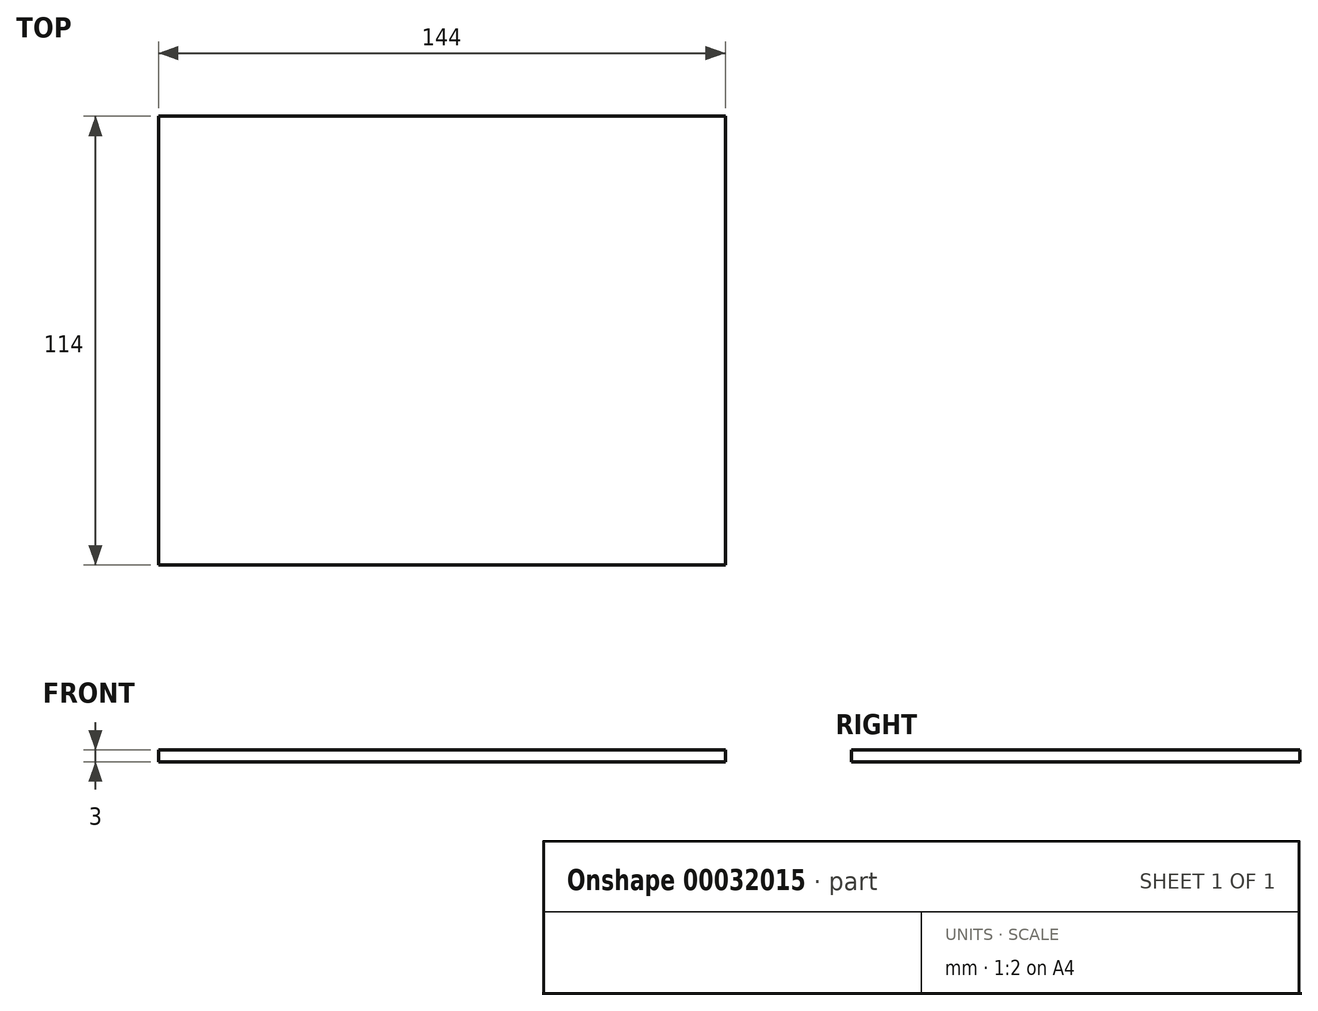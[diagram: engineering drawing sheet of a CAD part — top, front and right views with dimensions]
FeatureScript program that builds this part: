
annotation { "Feature Type Name" : "Feature", "Feature Type Description" : "" }
export const myFeature = defineFeature(function(context is Context, id is Id, definition is map)
    precondition{}
    {
        {
            var Q0;
            Q0=qCreatedBy(makeId("Top.planeOp"),FACE);
            var sketch = newSketch(context, id + "F0", { "sketchPlane" : qUnion([Q0])});
            skLineSegment(sketch, "E0.rect.bottom", {"start": v(72, -57) * mm, "end": v(-72, -57) * mm});
            skLineSegment(sketch, "E0.rect.top", {"start": v(72, 57) * mm, "end": v(-72, 57) * mm});
            skLineSegment(sketch, "E0.rect.left", {"start": v(72, -57) * mm, "end": v(72, 57) * mm});
            skLineSegment(sketch, "E0.rect.right", {"start": v(-72, -57) * mm, "end": v(-72, 57) * mm});
            skPoint(sketch, "E0.rect.middle", {"position": v(0, 0) * mm});
            skSolve(sketch);
        }
        {
            var Q0;
            Q0=makeQuery(id+"F0.imprint","IMPRINT",FACE,{"disambiguationData":[TD([[makeQuery(id+"F0.imprint","IMPRINT",EDGE,{"derivedFrom":sQuery(id+"F0.wireOp",EDGE,"E0.rect.bottom")}),-1.0]])]});
            extrude(context, id + "F1", {"entities" : qUnion([Q0]), "depth" : 3 * mm});
        }
    });
